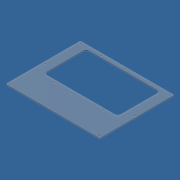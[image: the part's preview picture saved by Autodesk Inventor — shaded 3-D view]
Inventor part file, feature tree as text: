
AUTODESK INVENTOR PART (.ipt)
format: ipt  version: 2015 SP2 (Build 190223200, 223)  size: 149,504 bytes
history: native  units: mm (DEFAULTED — no unit token found)
features: other x8, sketch x2, hole x2, extrude x1, fillet x1
bodies: Solide1 (feature_tree)
feature tree (14):
  other  "Origine"
  sketch  "Esquisse1"
  extrude  "Extrusion1"  Depth=193.0mm
  hole  "Perçage6"  [1 undecoded]
  fillet  "Congé1"  Radius=8.0mm
  hole  "Perçage4"  [1 undecoded]
  other  "Plan YZ"
  other  "Plan XZ"
  other  "Plan XY"
  other  "Axe X"
  other  "Axe Y"
  other  "Axe Z"
  other  "Point de centre"
  sketch  "Esquisse9"
note: 2 required parameter values undecoded (feature->parameter linkage not recoverable at this tier; creation-order binding heuristic only, values carry confidence <= 0.55)
